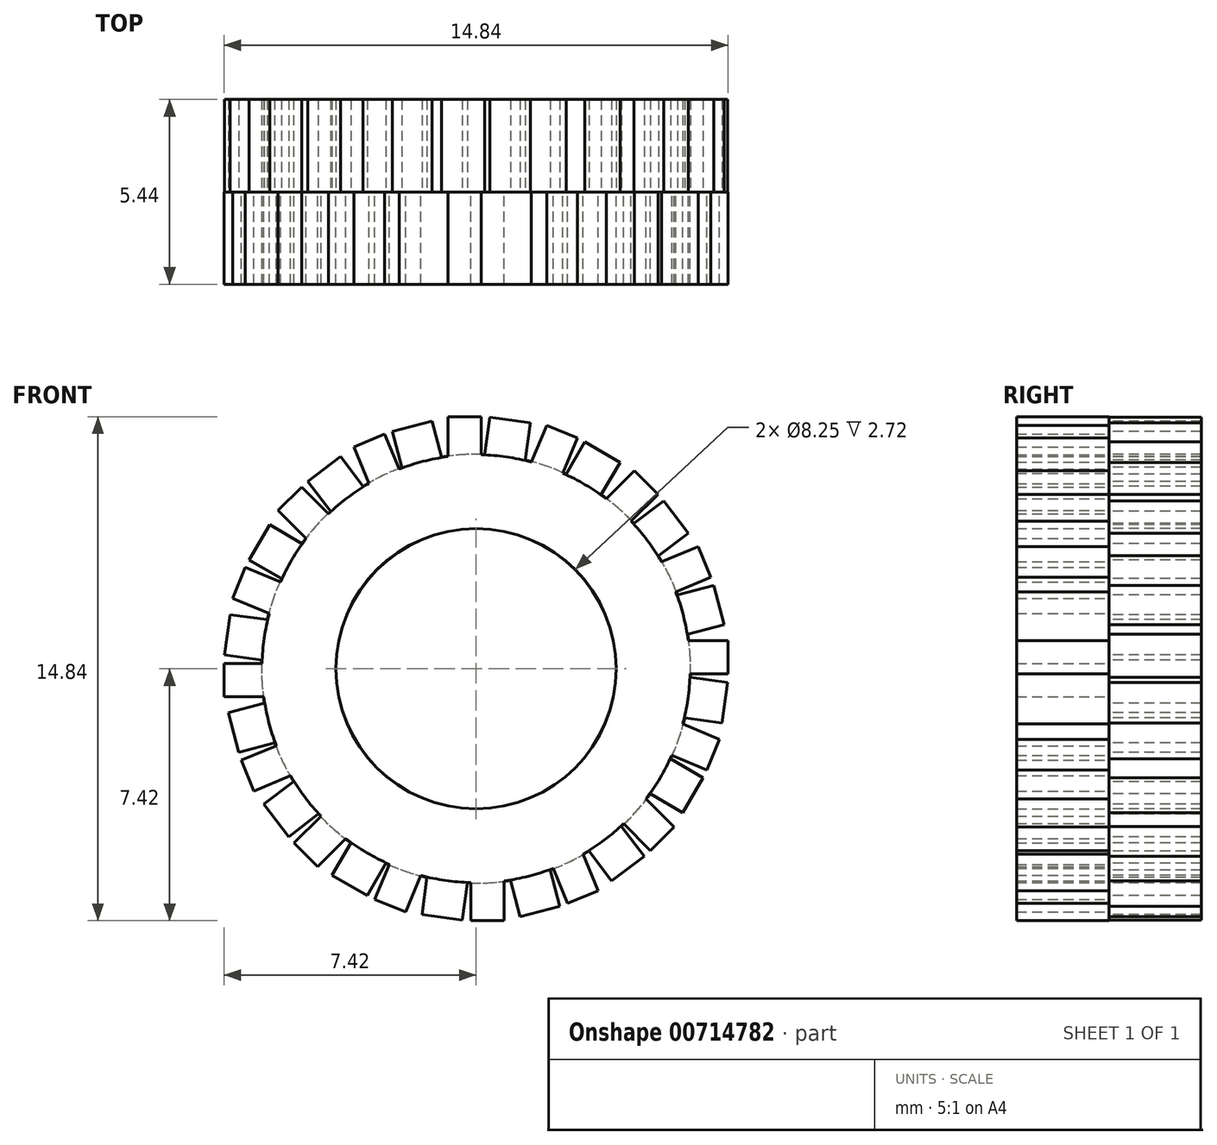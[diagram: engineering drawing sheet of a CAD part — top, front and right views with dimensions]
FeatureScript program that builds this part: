
annotation { "Feature Type Name" : "Feature", "Feature Type Description" : "" }
export const myFeature = defineFeature(function(context is Context, id is Id, definition is map)
    precondition{}
    {
        {
            var Q0;
            Q0=qCreatedBy(makeId("Front.planeOp"),FACE);
            var sketch = newSketch(context, id + "F0", { "sketchPlane" : qUnion([Q0])});
            skCircle(sketch, "E0", {"center": v(0, 0) * mm, "radius": 6.3 * mm});
            skCircle(sketch, "E1", {"center": v(0, 0) * mm, "radius": 4.12 * mm});
            skLineSegment(sketch, "E2.bottom", {"start": v(-0.82, 6.25) * mm, "end": v(0.16, 6.25) * mm});
            skLineSegment(sketch, "E2.top", {"start": v(-0.82, 7.42) * mm, "end": v(0.16, 7.42) * mm});
            skLineSegment(sketch, "E2.left", {"start": v(-0.82, 6.25) * mm, "end": v(-0.82, 7.42) * mm});
            skLineSegment(sketch, "E2.right", {"start": v(0.16, 6.25) * mm, "end": v(0.16, 7.42) * mm});
            skLineSegment(sketch, "E3.right", {"start": v(0.82, -6.23) * mm, "end": v(0.8, -6.25) * mm});
            skPoint(sketch, "E3.top.end.orphan", {"position": v(0.16, -7.38) * mm});
            skPoint(sketch, "E3.bottom.start.orphan", {"position": v(-0.82, -6.25) * mm});
            skPoint(sketch, "E4.start.orphan", {"position": v(-8.01, 0) * mm});
            skLineSegment(sketch, "E5.1.0", {"start": v(-2.25, 5.83) * mm, "end": v(-2.7, 6.91) * mm});
            skLineSegment(sketch, "E5.1.1", {"start": v(-3.6, 6.54) * mm, "end": v(-2.7, 6.91) * mm});
            skLineSegment(sketch, "E5.1.2", {"start": v(-3.15, 5.45) * mm, "end": v(-2.25, 5.83) * mm});
            skLineSegment(sketch, "E5.1.3", {"start": v(-3.15, 5.45) * mm, "end": v(-3.6, 6.54) * mm});
            skLineSegment(sketch, "E5.2.0", {"start": v(-4.3, 4.53) * mm, "end": v(-5.13, 5.35) * mm});
            skLineSegment(sketch, "E5.2.1", {"start": v(-5.83, 4.66) * mm, "end": v(-5.13, 5.35) * mm});
            skLineSegment(sketch, "E5.2.2", {"start": v(-5, 3.83) * mm, "end": v(-4.3, 4.53) * mm});
            skLineSegment(sketch, "E5.2.3", {"start": v(-5, 3.83) * mm, "end": v(-5.83, 4.66) * mm});
            skLineSegment(sketch, "E5.3.0", {"start": v(-5.71, 2.53) * mm, "end": v(-6.8, 2.98) * mm});
            skLineSegment(sketch, "E5.3.1", {"start": v(-7.17, 2.08) * mm, "end": v(-6.8, 2.98) * mm});
            skLineSegment(sketch, "E5.3.2", {"start": v(-6.09, 1.63) * mm, "end": v(-5.71, 2.53) * mm});
            skLineSegment(sketch, "E5.3.3", {"start": v(-6.09, 1.63) * mm, "end": v(-7.17, 2.08) * mm});
            skLineSegment(sketch, "E5.4.0", {"start": v(-6.25, 0.16) * mm, "end": v(-7.42, 0.16) * mm});
            skLineSegment(sketch, "E5.4.1", {"start": v(-7.42, -0.82) * mm, "end": v(-7.42, 0.16) * mm});
            skLineSegment(sketch, "E5.4.2", {"start": v(-6.25, -0.82) * mm, "end": v(-6.25, 0.16) * mm});
            skLineSegment(sketch, "E5.4.3", {"start": v(-6.25, -0.82) * mm, "end": v(-7.42, -0.82) * mm});
            skLineSegment(sketch, "E5.5.0", {"start": v(-5.83, -2.25) * mm, "end": v(-6.91, -2.7) * mm});
            skLineSegment(sketch, "E5.5.1", {"start": v(-6.54, -3.6) * mm, "end": v(-6.91, -2.7) * mm});
            skLineSegment(sketch, "E5.5.2", {"start": v(-5.45, -3.15) * mm, "end": v(-5.83, -2.25) * mm});
            skLineSegment(sketch, "E5.5.3", {"start": v(-5.45, -3.15) * mm, "end": v(-6.54, -3.6) * mm});
            skLineSegment(sketch, "E5.6.0", {"start": v(-4.53, -4.3) * mm, "end": v(-5.35, -5.13) * mm});
            skLineSegment(sketch, "E5.6.1", {"start": v(-4.66, -5.83) * mm, "end": v(-5.35, -5.13) * mm});
            skLineSegment(sketch, "E5.6.2", {"start": v(-3.83, -5) * mm, "end": v(-4.53, -4.3) * mm});
            skLineSegment(sketch, "E5.6.3", {"start": v(-3.83, -5) * mm, "end": v(-4.66, -5.83) * mm});
            skLineSegment(sketch, "E5.7.0", {"start": v(-2.53, -5.71) * mm, "end": v(-2.98, -6.8) * mm});
            skLineSegment(sketch, "E5.7.1", {"start": v(-2.08, -7.17) * mm, "end": v(-2.98, -6.8) * mm});
            skLineSegment(sketch, "E5.7.2", {"start": v(-1.63, -6.09) * mm, "end": v(-2.53, -5.71) * mm});
            skLineSegment(sketch, "E5.7.3", {"start": v(-1.63, -6.09) * mm, "end": v(-2.08, -7.17) * mm});
            skLineSegment(sketch, "E5.8.0", {"start": v(-0.16, -6.25) * mm, "end": v(-0.16, -7.42) * mm});
            skLineSegment(sketch, "E5.8.1", {"start": v(0.82, -7.42) * mm, "end": v(-0.16, -7.42) * mm});
            skLineSegment(sketch, "E5.8.2", {"start": v(0.82, -6.25) * mm, "end": v(-0.16, -6.25) * mm});
            skLineSegment(sketch, "E5.8.3", {"start": v(0.82, -6.25) * mm, "end": v(0.82, -7.42) * mm});
            skLineSegment(sketch, "E5.9.0", {"start": v(2.25, -5.83) * mm, "end": v(2.7, -6.91) * mm});
            skLineSegment(sketch, "E5.9.1", {"start": v(3.6, -6.54) * mm, "end": v(2.7, -6.91) * mm});
            skLineSegment(sketch, "E5.9.2", {"start": v(3.15, -5.45) * mm, "end": v(2.25, -5.83) * mm});
            skLineSegment(sketch, "E5.9.3", {"start": v(3.15, -5.45) * mm, "end": v(3.6, -6.54) * mm});
            skLineSegment(sketch, "E5.10.0", {"start": v(4.3, -4.53) * mm, "end": v(5.13, -5.35) * mm});
            skLineSegment(sketch, "E5.10.1", {"start": v(5.83, -4.66) * mm, "end": v(5.13, -5.35) * mm});
            skLineSegment(sketch, "E5.10.2", {"start": v(5, -3.83) * mm, "end": v(4.3, -4.53) * mm});
            skLineSegment(sketch, "E5.10.3", {"start": v(5, -3.83) * mm, "end": v(5.83, -4.66) * mm});
            skLineSegment(sketch, "E5.11.0", {"start": v(5.71, -2.53) * mm, "end": v(6.8, -2.98) * mm});
            skLineSegment(sketch, "E5.11.1", {"start": v(7.17, -2.08) * mm, "end": v(6.8, -2.98) * mm});
            skLineSegment(sketch, "E5.11.2", {"start": v(6.09, -1.63) * mm, "end": v(5.71, -2.53) * mm});
            skLineSegment(sketch, "E5.11.3", {"start": v(6.09, -1.63) * mm, "end": v(7.17, -2.08) * mm});
            skLineSegment(sketch, "E5.12.0", {"start": v(6.25, -0.16) * mm, "end": v(7.42, -0.16) * mm});
            skLineSegment(sketch, "E5.12.1", {"start": v(7.42, 0.82) * mm, "end": v(7.42, -0.16) * mm});
            skLineSegment(sketch, "E5.12.2", {"start": v(6.25, 0.82) * mm, "end": v(6.25, -0.16) * mm});
            skLineSegment(sketch, "E5.12.3", {"start": v(6.25, 0.82) * mm, "end": v(7.42, 0.82) * mm});
            skLineSegment(sketch, "E5.13.0", {"start": v(5.83, 2.25) * mm, "end": v(6.91, 2.7) * mm});
            skLineSegment(sketch, "E5.13.1", {"start": v(6.54, 3.6) * mm, "end": v(6.91, 2.7) * mm});
            skLineSegment(sketch, "E5.13.2", {"start": v(5.45, 3.15) * mm, "end": v(5.83, 2.25) * mm});
            skLineSegment(sketch, "E5.13.3", {"start": v(5.45, 3.15) * mm, "end": v(6.54, 3.6) * mm});
            skLineSegment(sketch, "E5.14.0", {"start": v(4.53, 4.3) * mm, "end": v(5.35, 5.13) * mm});
            skLineSegment(sketch, "E5.14.1", {"start": v(4.66, 5.83) * mm, "end": v(5.35, 5.13) * mm});
            skLineSegment(sketch, "E5.14.2", {"start": v(3.83, 5) * mm, "end": v(4.53, 4.3) * mm});
            skLineSegment(sketch, "E5.14.3", {"start": v(3.83, 5) * mm, "end": v(4.66, 5.83) * mm});
            skLineSegment(sketch, "E5.15.0", {"start": v(2.53, 5.71) * mm, "end": v(2.98, 6.8) * mm});
            skLineSegment(sketch, "E5.15.1", {"start": v(2.08, 7.17) * mm, "end": v(2.98, 6.8) * mm});
            skLineSegment(sketch, "E5.15.2", {"start": v(1.63, 6.09) * mm, "end": v(2.53, 5.71) * mm});
            skLineSegment(sketch, "E5.15.3", {"start": v(1.63, 6.09) * mm, "end": v(2.08, 7.17) * mm});
            skSolve(sketch);
        }
        {
            var Q0;
            Q0 = qSketchRegion(id + "F0", true);
            extrude(context, id + "F1", {"entities" : qUnion([Q0]), "depth" : 2.72 * mm, "offsetDistance" : 25 * mm});
        }
        {
            var Q0;
            Q0=qCreatedBy(makeId("Front.planeOp"),FACE);
            var sketch = newSketch(context, id + "F2", { "sketchPlane" : qUnion([Q0])});
            skCircle(sketch, "E6", {"center": v(0, 0) * mm, "radius": 4.12 * mm});
            skCircle(sketch, "E7", {"center": v(0, 0) * mm, "radius": 6.32 * mm});
            skLineSegment(sketch, "E8", {"start": v(-2.18, 5.93) * mm, "end": v(-2.46, 7) * mm});
            skLineSegment(sketch, "E9", {"start": v(-2.46, 7) * mm, "end": v(-1.3, 7.3) * mm});
            skLineSegment(sketch, "E10", {"start": v(-1.3, 7.3) * mm, "end": v(-1.02, 6.23) * mm});
            skLineSegment(sketch, "E11.1.0", {"start": v(-4.95, 5.52) * mm, "end": v(-4, 6.24) * mm});
            skLineSegment(sketch, "E11.1.1", {"start": v(-4, 6.24) * mm, "end": v(-3.33, 5.37) * mm});
            skLineSegment(sketch, "E11.1.2", {"start": v(-4.28, 4.64) * mm, "end": v(-4.95, 5.52) * mm});
            skLineSegment(sketch, "E11.2.0", {"start": v(-6.68, 3.2) * mm, "end": v(-6.08, 4.24) * mm});
            skLineSegment(sketch, "E11.2.1", {"start": v(-6.08, 4.24) * mm, "end": v(-5.13, 3.69) * mm});
            skLineSegment(sketch, "E11.2.2", {"start": v(-5.73, 2.65) * mm, "end": v(-6.68, 3.2) * mm});
            skLineSegment(sketch, "E11.3.0", {"start": v(-7.4, 0.4) * mm, "end": v(-7.24, 1.6) * mm});
            skLineSegment(sketch, "E11.3.1", {"start": v(-7.24, 1.6) * mm, "end": v(-6.15, 1.44) * mm});
            skLineSegment(sketch, "E11.3.2", {"start": v(-6.31, 0.26) * mm, "end": v(-7.4, 0.4) * mm});
            skLineSegment(sketch, "E11.4.0", {"start": v(-7, -2.46) * mm, "end": v(-7.3, -1.3) * mm});
            skLineSegment(sketch, "E11.4.1", {"start": v(-7.3, -1.3) * mm, "end": v(-6.23, -1.02) * mm});
            skLineSegment(sketch, "E11.4.2", {"start": v(-5.93, -2.18) * mm, "end": v(-7, -2.46) * mm});
            skLineSegment(sketch, "E11.5.0", {"start": v(-5.52, -4.95) * mm, "end": v(-6.24, -4) * mm});
            skLineSegment(sketch, "E11.5.1", {"start": v(-6.24, -4) * mm, "end": v(-5.37, -3.33) * mm});
            skLineSegment(sketch, "E11.5.2", {"start": v(-4.64, -4.28) * mm, "end": v(-5.52, -4.95) * mm});
            skLineSegment(sketch, "E11.6.0", {"start": v(-3.2, -6.68) * mm, "end": v(-4.24, -6.08) * mm});
            skLineSegment(sketch, "E11.6.1", {"start": v(-4.24, -6.08) * mm, "end": v(-3.69, -5.13) * mm});
            skLineSegment(sketch, "E11.6.2", {"start": v(-2.65, -5.73) * mm, "end": v(-3.2, -6.68) * mm});
            skLineSegment(sketch, "E11.7.0", {"start": v(-0.4, -7.4) * mm, "end": v(-1.6, -7.24) * mm});
            skLineSegment(sketch, "E11.7.1", {"start": v(-1.6, -7.24) * mm, "end": v(-1.44, -6.15) * mm});
            skLineSegment(sketch, "E11.7.2", {"start": v(-0.26, -6.31) * mm, "end": v(-0.4, -7.4) * mm});
            skLineSegment(sketch, "E11.8.0", {"start": v(2.46, -7) * mm, "end": v(1.3, -7.3) * mm});
            skLineSegment(sketch, "E11.8.1", {"start": v(1.3, -7.3) * mm, "end": v(1.02, -6.23) * mm});
            skLineSegment(sketch, "E11.8.2", {"start": v(2.18, -5.93) * mm, "end": v(2.46, -7) * mm});
            skLineSegment(sketch, "E11.9.0", {"start": v(4.95, -5.52) * mm, "end": v(4, -6.24) * mm});
            skLineSegment(sketch, "E11.9.1", {"start": v(4, -6.24) * mm, "end": v(3.33, -5.37) * mm});
            skLineSegment(sketch, "E11.9.2", {"start": v(4.28, -4.64) * mm, "end": v(4.95, -5.52) * mm});
            skLineSegment(sketch, "E11.10.0", {"start": v(6.68, -3.2) * mm, "end": v(6.08, -4.24) * mm});
            skLineSegment(sketch, "E11.10.1", {"start": v(6.08, -4.24) * mm, "end": v(5.13, -3.69) * mm});
            skLineSegment(sketch, "E11.10.2", {"start": v(5.73, -2.65) * mm, "end": v(6.68, -3.2) * mm});
            skLineSegment(sketch, "E11.11.0", {"start": v(7.4, -0.4) * mm, "end": v(7.24, -1.6) * mm});
            skLineSegment(sketch, "E11.11.1", {"start": v(7.24, -1.6) * mm, "end": v(6.15, -1.44) * mm});
            skLineSegment(sketch, "E11.11.2", {"start": v(6.31, -0.26) * mm, "end": v(7.4, -0.4) * mm});
            skLineSegment(sketch, "E11.12.0", {"start": v(7, 2.46) * mm, "end": v(7.3, 1.3) * mm});
            skLineSegment(sketch, "E11.12.1", {"start": v(7.3, 1.3) * mm, "end": v(6.23, 1.02) * mm});
            skLineSegment(sketch, "E11.12.2", {"start": v(5.93, 2.18) * mm, "end": v(7, 2.46) * mm});
            skLineSegment(sketch, "E11.13.0", {"start": v(5.52, 4.95) * mm, "end": v(6.24, 4) * mm});
            skLineSegment(sketch, "E11.13.1", {"start": v(6.24, 4) * mm, "end": v(5.37, 3.33) * mm});
            skLineSegment(sketch, "E11.13.2", {"start": v(4.64, 4.28) * mm, "end": v(5.52, 4.95) * mm});
            skLineSegment(sketch, "E11.14.0", {"start": v(3.2, 6.68) * mm, "end": v(4.24, 6.08) * mm});
            skLineSegment(sketch, "E11.14.1", {"start": v(4.24, 6.08) * mm, "end": v(3.69, 5.13) * mm});
            skLineSegment(sketch, "E11.14.2", {"start": v(2.65, 5.73) * mm, "end": v(3.2, 6.68) * mm});
            skLineSegment(sketch, "E11.15.0", {"start": v(0.4, 7.4) * mm, "end": v(1.6, 7.24) * mm});
            skLineSegment(sketch, "E11.15.1", {"start": v(1.6, 7.24) * mm, "end": v(1.44, 6.15) * mm});
            skLineSegment(sketch, "E11.15.2", {"start": v(0.26, 6.31) * mm, "end": v(0.4, 7.4) * mm});
            skSolve(sketch);
        }
        {
            var Q0;
            Q0 = qSketchRegion(id + "F2", true);
            extrude(context, id + "F3", {"entities" : qUnion([Q0]), "operationType" : NewBodyOperationType.ADD, "oppositeDirection" : true, "depth" : 2.72 * mm, "offsetDistance" : 25 * mm});
        }
    });
